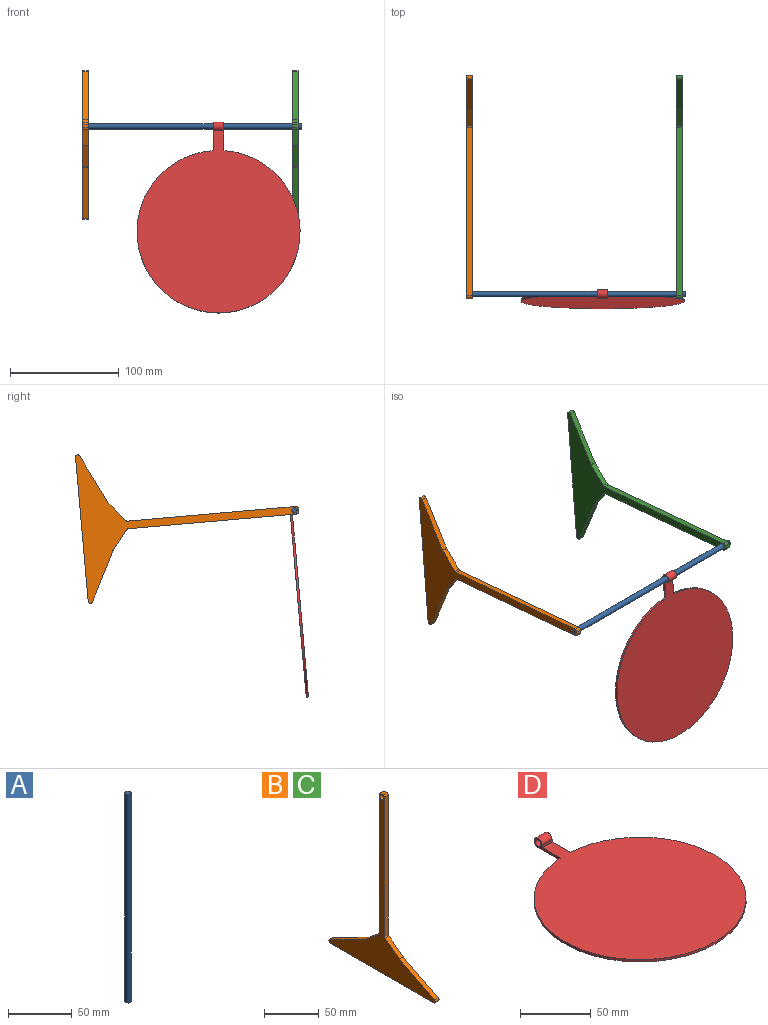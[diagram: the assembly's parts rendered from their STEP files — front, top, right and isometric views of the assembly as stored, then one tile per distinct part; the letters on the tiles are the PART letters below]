
ASSEMBLY  parts=4 mates=4
PART A: 3 faces, bbox 5x5x200 mm
  f0: cylinder r=2.5mm len=200mm, axis (0,0,-1), area 3141.6mm2, adj f1,f2
  f1: plane 5x5mm, normal (0,0,1), area 19.6mm2, adj f0
  f2: plane 5x5mm, normal (0,0,-1), area 19.6mm2, adj f0
PART B: 19 faces, bbox 5x137.1x200 mm
  f0: plane 5x3mm, normal (0,0,1), area 15mm2, adj f8,f9,f11,f13
  f1: plane 155.37x5mm, normal (0,-1,0), area 776.8mm2, adj f8,f9,f12,f13
  f2: plane 18.22x14.24mm, normal (0,-0.62,0.79), area 115.6mm2, adj f8,f9,f12,f14
  f3: plane 45.03x22.82mm, normal (0,-0.45,0.89), area 252.4mm2, adj f8,f9,f14,f15
  f4: plane 133.13x5mm, normal (0,0,-1), area 665.7mm2, adj f8,f9,f15,f16
  f5: plane 45.73x22.79mm, normal (0,0.45,0.89), area 255.5mm2, adj f8,f9,f16,f17
  f6: plane 16.75x14.21mm, normal (0,0.65,0.76), area 109.8mm2, adj f8,f9,f10,f17
  f7: plane 155.42x5mm, normal (0,1,0), area 777.1mm2, adj f8,f9,f10,f11
  f8: plane 200x137.13mm, normal (1,0,0), area 4030.3mm2, adj f0,f1,f2,f3,f4,f5,f6,f7
  f9: plane 200x137.13mm, normal (-1,0,0), area 4030.3mm2, adj f0,f1,f2,f3,f4,f5,f6,f7
  f10: cylinder r=2mm len=5mm, axis (1,0,0), area 8.7mm2, adj f6,f7,f8,f9
  f11: cylinder r=2mm len=5mm, axis (-1,0,0), area 15.7mm2, adj f0,f7,f8,f9
  f12: cylinder r=2mm len=5mm, axis (-1,0,0), area 9.1mm2, adj f1,f2,f8,f9
  f13: cylinder r=2mm len=5mm, axis (1,0,0), area 15.7mm2, adj f0,f1,f8,f9
  f14: cylinder r=2mm len=5mm, axis (-1,0,0), area 1.9mm2, adj f2,f3,f8,f9
  f15: cylinder r=2mm len=5mm, axis (-1,0,0), area 26.7mm2, adj f3,f4,f8,f9
  f16: cylinder r=2mm len=5mm, axis (1,0,0), area 26.8mm2, adj f4,f5,f8,f9
  f17: cylinder r=2mm len=5mm, axis (1,0,0), area 2.4mm2, adj f5,f6,f8,f9
  f18: cylinder r=2.5mm len=5mm, axis (1,0,0), area 78.5mm2, adj f8,f9
PART C: same geometry as B
PART D: 8 faces, bbox 150x176x8 mm
  f0: plane 26.17x8mm, normal (-1,0,0), area 68mm2, adj f1,f2,f3,f5,f6,f7
  f1: plane 172x150mm, normal (0,0,-1), area 17892mm2, adj f0,f2,f4,f5
  f2: cylinder r=4mm len=10mm, axis (1,0,0), area 185.7mm2, adj f0,f1,f3,f4
  f3: plane 10x2.28mm, normal (0,-1,0), area 22.8mm2, adj f0,f2,f4,f6
  f4: plane 26.17x8mm, normal (1,0,0), area 68mm2, adj f1,f2,f3,f5,f6,f7
  f5: cylinder r=75mm len=150mm, axis (0,0,-1), area 922.5mm2, adj f0,f1,f4,f6
  f6: plane 168x150mm, normal (0,0,1), area 17852mm2, adj f0,f3,f4,f5
  f7: cylinder r=2.65mm len=10mm, axis (-1,0,0), area 166.5mm2, adj f0,f4
PLACE A rot(axis=(0.56,-0.61,-0.56),117.2deg) t=(6.24,-121.3,186.5)mm
PLACE B rot(axis=(1,0,0),85deg) t=(-194.64,121.01,108.05)mm
PLACE C rot(axis=(1,0,0),85deg) t=(-1.67,121.01,108.05)mm
PLACE D rot(axis=(1,0,0),85deg) t=(-69.79,-78.83,28.17)mm
MATE slider A.f0 <-> B.f18  axis (1,0,0) through (-93.76,-74.36,125.15)mm
MATE slider C.f18 <-> A.f0  axis (1,0,0) through (3.33,-74.36,125.15)mm
MATE slider A.f0 <-> D.f2  axis (1,0,0) through (-93.76,-74.36,125.15)mm
MATE parallel A.f0 <-> C.f8  axis (1,0,0) through (6.24,-74.36,125.15)mm
